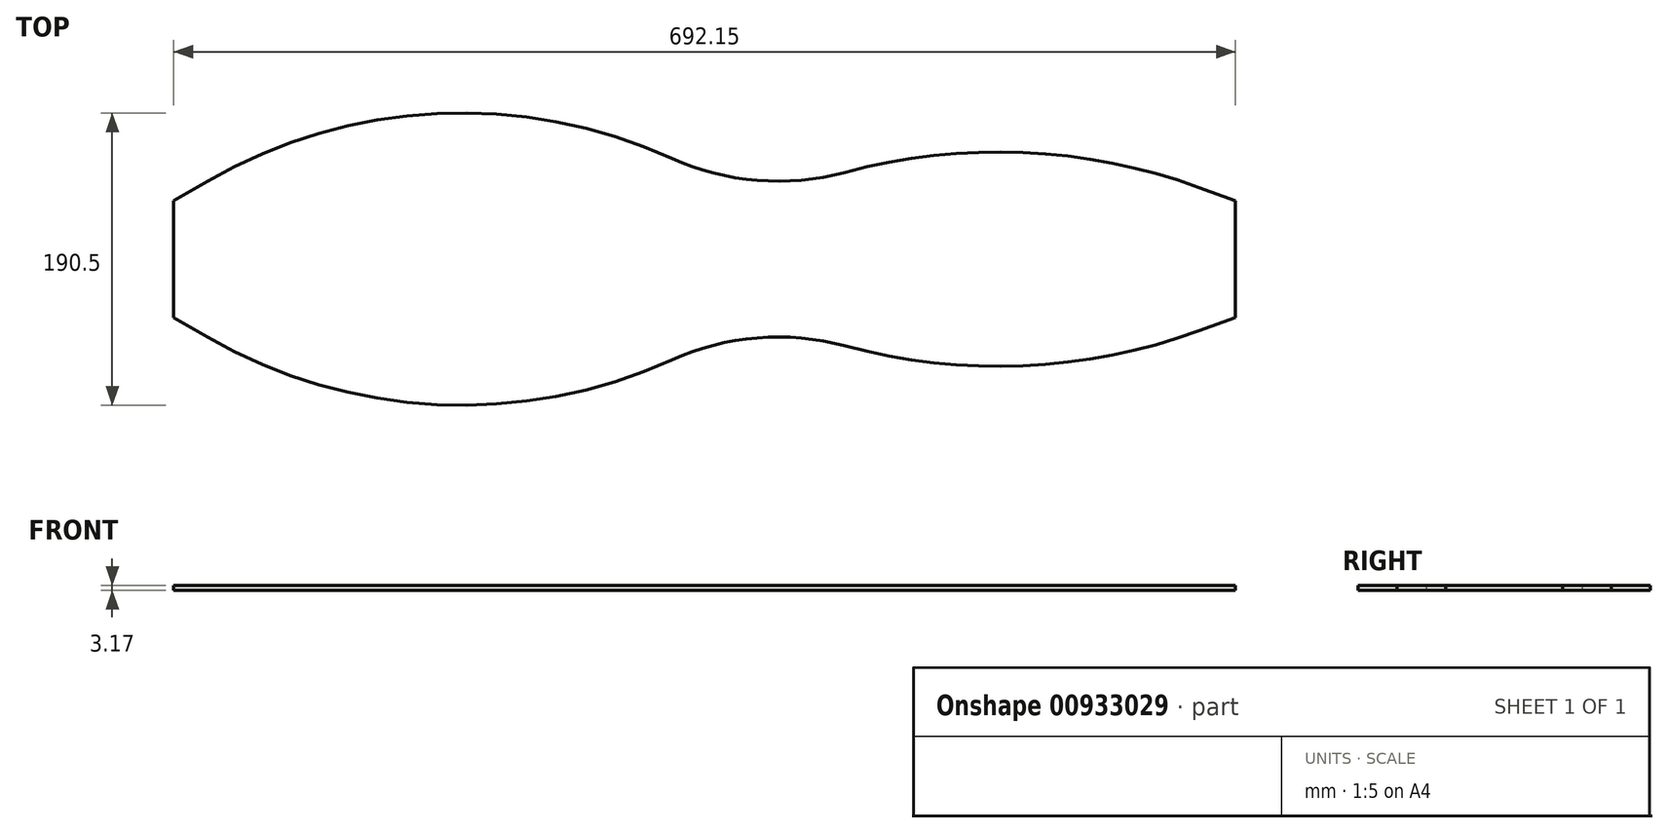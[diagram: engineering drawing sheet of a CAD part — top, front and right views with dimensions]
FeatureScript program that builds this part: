
annotation { "Feature Type Name" : "Feature", "Feature Type Description" : "" }
export const myFeature = defineFeature(function(context is Context, id is Id, definition is map)
    precondition{}
    {
        {
            var Q0;
            Q0=qCreatedBy(makeId("Top.planeOp"),FACE);
            var sketch = newSketch(context, id + "F0", { "sketchPlane" : qUnion([Q0])});
            skLineSegment(sketch, "E0.bottom", {"start": v(0, 0) * mm, "end": v(692.15, 0) * mm});
            skLineSegment(sketch, "E0.left", {"start": v(0, 0) * mm, "end": v(0, -38.1) * mm});
            skLineSegment(sketch, "E0.right", {"start": v(692.15, 0) * mm, "end": v(692.15, -38.1) * mm});
            skLineSegment(sketch, "E1", {"start": v(0, -38.1) * mm, "end": v(22, -50.8) * mm});
            skLineSegment(sketch, "E2", {"start": v(692.15, -38.1) * mm, "end": v(668.28, -46.79) * mm});
            skArc(sketch, "E3", {"start": v(22, -50.8) * mm, "mid": v(171.53, -94.85) * mm, "end": v(324.67, -65.74) * mm});
            skArc(sketch, "E4", {"start": v(668.28, -46.79) * mm, "mid": v(553.77, -69.5) * mm, "end": v(437.75, -56.61) * mm});
            skArc(sketch, "E5", {"start": v(324.67, -65.74) * mm, "mid": v(407.45, -386.25) * mm, "end": v(437.75, -56.61) * mm, "construction": true});
            skLineSegment(sketch, "E6", {"start": v(187.89, 236.53) * mm, "end": v(187.89, -95.25) * mm, "construction": true});
            skLineSegment(sketch, "E7", {"start": v(537.49, 312.57) * mm, "end": v(537.49, -69.85) * mm, "construction": true});
            skLineSegment(sketch, "E8", {"start": v(393.93, -218.8) * mm, "end": v(393.93, -50.8) * mm, "construction": true});
            skArc(sketch, "E9", {"start": v(324.67, -65.74) * mm, "mid": v(380.42, -51.34) * mm, "end": v(437.75, -56.61) * mm});
            skSolve(sketch);
        }
        {
            var Q0;
            Q0=qSketchRegion(id+"F0",true);
            extrude(context, id + "F1", {"entities" : qUnion([Q0]), "depth" : 3.17 * mm});
        }
        {
            var Q0;
            Q0=makeQuery(id+"F1.opExtrude","SWEPT_BODY",BODY,{"disambiguationData":[OSD([sQuery(id+"F0.wireOp",EDGE,"E0.bottom"),sQuery(id+"F0.wireOp",EDGE,"E0.left"),sQuery(id+"F0.wireOp",EDGE,"E0.right"),sQuery(id+"F0.wireOp",EDGE,"E1"),sQuery(id+"F0.wireOp",EDGE,"E2"),sQuery(id+"F0.wireOp",EDGE,"E3"),sQuery(id+"F0.wireOp",EDGE,"E4"),sQuery(id+"F0.wireOp",EDGE,"E9")])]});
            var Q1;
            Q1=qCreatedBy(makeId("Front.planeOp"),FACE);
            mirror(context, id + "F2", {"operationType" : NewBodyOperationType.ADD, "entities" : qUnion([Q0]), "mirrorPlane" : qUnion([Q1])});
        }
    });
